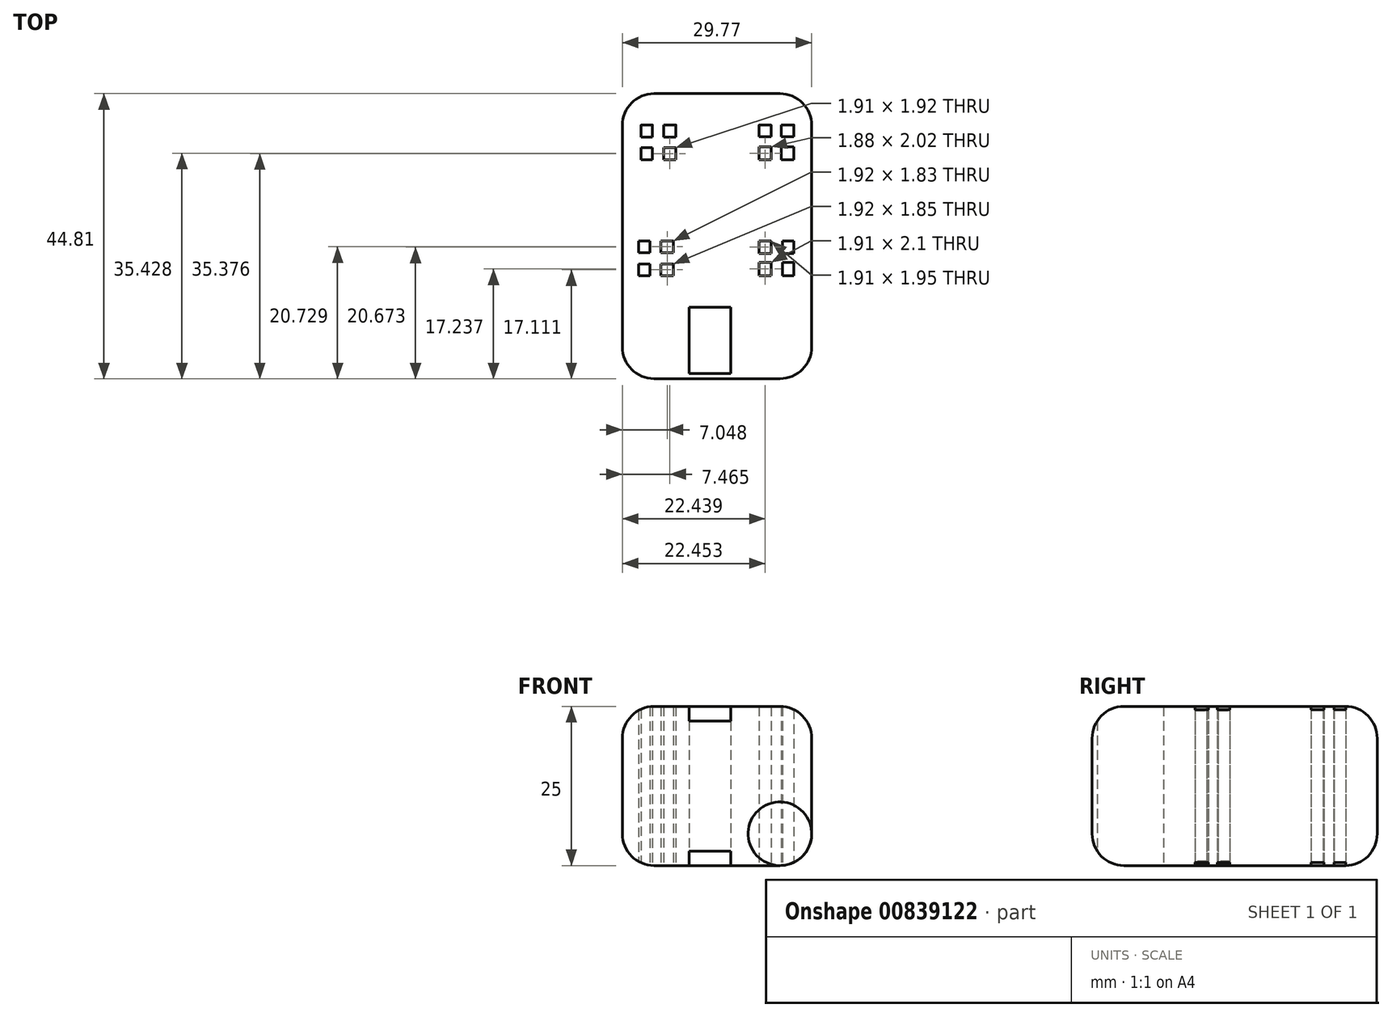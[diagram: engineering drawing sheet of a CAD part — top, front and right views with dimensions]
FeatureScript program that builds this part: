
annotation { "Feature Type Name" : "Feature", "Feature Type Description" : "" }
export const myFeature = defineFeature(function(context is Context, id is Id, definition is map)
    precondition{}
    {
        {
            var Q0;
            Q0=qCreatedBy(makeId("Top.planeOp"),FACE);
            var sketch = newSketch(context, id + "F0", { "sketchPlane" : qUnion([Q0])});
            skLineSegment(sketch, "E0", {"start": v(-55.24, 44.8) * mm, "end": v(-55.24, 0) * mm});
            skLineSegment(sketch, "E1", {"start": v(-55.24, 0) * mm, "end": v(-25.47, 0) * mm});
            skLineSegment(sketch, "E2", {"start": v(-25.47, 0) * mm, "end": v(-25.47, 44.2) * mm});
            skLineSegment(sketch, "E3", {"start": v(-55.24, 44.8) * mm, "end": v(-25.47, 44.8) * mm});
            skLineSegment(sketch, "E4", {"start": v(-25.47, 44.8) * mm, "end": v(-25.47, 44.2) * mm});
            skLineSegment(sketch, "E5.bottom", {"start": v(-44.76, 11.24) * mm, "end": v(-38.17, 11.24) * mm});
            skLineSegment(sketch, "E5.top", {"start": v(-44.76, 0) * mm, "end": v(-38.17, 0) * mm});
            skLineSegment(sketch, "E5.left", {"start": v(-44.76, 11.24) * mm, "end": v(-44.76, 0) * mm});
            skLineSegment(sketch, "E5.right", {"start": v(-38.17, 11.24) * mm, "end": v(-38.17, 0) * mm});
            skLineSegment(sketch, "E6.bottom", {"start": v(-52.28, 39.88) * mm, "end": v(-46.82, 39.88) * mm});
            skLineSegment(sketch, "E6.top", {"start": v(-52.28, 34.42) * mm, "end": v(-46.82, 34.42) * mm});
            skLineSegment(sketch, "E6.left", {"start": v(-52.28, 39.88) * mm, "end": v(-52.28, 34.42) * mm});
            skLineSegment(sketch, "E6.right", {"start": v(-46.82, 39.88) * mm, "end": v(-46.82, 34.42) * mm});
            skLineSegment(sketch, "E7.bottom", {"start": v(-28.28, 39.88) * mm, "end": v(-33.74, 39.88) * mm});
            skLineSegment(sketch, "E7.top", {"start": v(-28.28, 34.42) * mm, "end": v(-33.74, 34.42) * mm});
            skLineSegment(sketch, "E7.left", {"start": v(-28.28, 39.88) * mm, "end": v(-28.28, 34.42) * mm});
            skLineSegment(sketch, "E7.right", {"start": v(-33.74, 39.88) * mm, "end": v(-33.74, 34.42) * mm});
            skLineSegment(sketch, "E8.bottom", {"start": v(-52.7, 21.65) * mm, "end": v(-47.23, 21.65) * mm});
            skLineSegment(sketch, "E8.top", {"start": v(-52.7, 16.19) * mm, "end": v(-47.23, 16.19) * mm});
            skLineSegment(sketch, "E8.left", {"start": v(-52.7, 21.65) * mm, "end": v(-52.7, 16.19) * mm});
            skLineSegment(sketch, "E8.right", {"start": v(-47.23, 21.65) * mm, "end": v(-47.23, 16.19) * mm});
            skLineSegment(sketch, "E9.bottom", {"start": v(-28.28, 21.65) * mm, "end": v(-33.74, 21.65) * mm});
            skLineSegment(sketch, "E9.top", {"start": v(-28.28, 16.19) * mm, "end": v(-33.74, 16.19) * mm});
            skLineSegment(sketch, "E9.left", {"start": v(-28.28, 21.65) * mm, "end": v(-28.28, 16.19) * mm});
            skLineSegment(sketch, "E9.right", {"start": v(-33.74, 21.65) * mm, "end": v(-33.74, 16.19) * mm});
            skLineSegment(sketch, "E10.bottom", {"start": v(-49.55, 39.88) * mm, "end": v(-49.55, 39.88) * mm});
            skLineSegment(sketch, "E10.top", {"start": v(-49.55, 34.42) * mm, "end": v(-49.55, 34.42) * mm});
            skLineSegment(sketch, "E11.left", {"start": v(-52.28, 37.15) * mm, "end": v(-52.28, 37.15) * mm});
            skLineSegment(sketch, "E11.right", {"start": v(-46.82, 37.15) * mm, "end": v(-46.82, 37.15) * mm});
            skLineSegment(sketch, "E12", {"start": v(-50.88, 21.65) * mm, "end": v(-50.88, 16.19) * mm});
            skLineSegment(sketch, "E13", {"start": v(-50.88, 16.19) * mm, "end": v(-49.15, 16.19) * mm});
            skLineSegment(sketch, "E14", {"start": v(-49.15, 16.19) * mm, "end": v(-49.15, 21.65) * mm});
            skLineSegment(sketch, "E15", {"start": v(-50.5, 39.88) * mm, "end": v(-50.5, 34.42) * mm});
            skLineSegment(sketch, "E16", {"start": v(-50.5, 34.42) * mm, "end": v(-48.73, 34.42) * mm});
            skLineSegment(sketch, "E17", {"start": v(-48.73, 34.42) * mm, "end": v(-48.73, 39.88) * mm});
            skLineSegment(sketch, "E18", {"start": v(-31.86, 39.88) * mm, "end": v(-31.86, 34.42) * mm});
            skLineSegment(sketch, "E19", {"start": v(-31.86, 34.42) * mm, "end": v(-30.23, 34.42) * mm});
            skLineSegment(sketch, "E20", {"start": v(-30.23, 34.42) * mm, "end": v(-30.23, 39.88) * mm});
            skLineSegment(sketch, "E21", {"start": v(-31.83, 21.65) * mm, "end": v(-31.83, 16.19) * mm});
            skLineSegment(sketch, "E22", {"start": v(-31.83, 16.19) * mm, "end": v(-30.07, 16.19) * mm});
            skLineSegment(sketch, "E23", {"start": v(-30.07, 16.19) * mm, "end": v(-30.07, 21.65) * mm});
            skLineSegment(sketch, "E24", {"start": v(-52.28, 37.94) * mm, "end": v(-46.82, 37.94) * mm});
            skLineSegment(sketch, "E25", {"start": v(-46.82, 36.33) * mm, "end": v(-52.28, 36.33) * mm});
            skLineSegment(sketch, "E26", {"start": v(-33.74, 38) * mm, "end": v(-28.28, 38) * mm});
            skLineSegment(sketch, "E27", {"start": v(-28.28, 38) * mm, "end": v(-28.28, 36.44) * mm});
            skLineSegment(sketch, "E28", {"start": v(-28.28, 36.44) * mm, "end": v(-33.74, 36.44) * mm});
            skLineSegment(sketch, "E29", {"start": v(-33.74, 36.44) * mm, "end": v(-33.67, 36.53) * mm});
            skLineSegment(sketch, "E30", {"start": v(-33.74, 19.7) * mm, "end": v(-28.28, 19.7) * mm});
            skLineSegment(sketch, "E31", {"start": v(-28.28, 19.7) * mm, "end": v(-28.28, 18.29) * mm});
            skLineSegment(sketch, "E32", {"start": v(-28.28, 18.29) * mm, "end": v(-33.74, 18.29) * mm});
            skLineSegment(sketch, "E33", {"start": v(-52.7, 19.81) * mm, "end": v(-47.23, 19.81) * mm});
            skLineSegment(sketch, "E34", {"start": v(-52.7, 18.04) * mm, "end": v(-47.23, 18.04) * mm});
            skPoint(sketch, "E35.startSnap0", {"position": v(-40.36, 44.8) * mm});
            skLineSegment(sketch, "E36", {"start": v(-44.76, 0.8) * mm, "end": v(-38.17, 0.8) * mm});
            skSolve(sketch);
        }
        {
            var Q0;
            {var subQ47=sQuery(id+"F0.wireOp",EDGE,"E36");var subQ54=sQuery(id+"F0.wireOp",EDGE,"E0");Q0=qUnion([makeQuery(id+"F0.imprint","IMPRINT",FACE,{"disambiguationData":[TD([[makeQuery(id+"F0.imprint","IMPRINT",EDGE,{"derivedFrom":subQ47}),-1.0]])]}),makeQuery(id+"F0.imprint","IMPRINT",FACE,{"disambiguationData":[TD([[makeQuery(id+"F0.imprint","IMPRINT",EDGE,{"derivedFrom":subQ54}),1.0]])]})]);}
            var Q1;
            {var subQ0=sQuery(id+"F0.wireOp",EDGE,"E32");var subQ1=sQuery(id+"F0.wireOp",EDGE,"E21");var subQ2=makeQuery(id+"F0.imprint","INTERSECT",VERTEX,{"derivedFrom":[subQ1,subQ0]});Q1=makeQuery(id+"F0.imprint","IMPRINT",FACE,{"disambiguationData":[TD([[makeQuery(id+"F0.imprint","IMPRINT",EDGE,{"disambiguationData":[TD([[subQ2,1.0]])],"derivedFrom":subQ1}),1.0]])]});}
            var Q2;
            {var subQ0=sQuery(id+"F0.wireOp",EDGE,"E21");var subQ1=sQuery(id+"F0.wireOp",EDGE,"E9.top");var subQ2=makeQuery(id+"F0.imprint","INTERSECT",VERTEX,{"derivedFrom":[subQ1,subQ0]});Q2=makeQuery(id+"F0.imprint","IMPRINT",FACE,{"disambiguationData":[TD([[makeQuery(id+"F0.imprint","IMPRINT",EDGE,{"disambiguationData":[TD([[subQ2,1.0]])],"derivedFrom":subQ1}),-1.0]])]});}
            var Q3;
            {var subQ0=sQuery(id+"F0.wireOp",EDGE,"E32");var subQ1=sQuery(id+"F0.wireOp",EDGE,"E9.right");var subQ2=makeQuery(id+"F0.imprint","INTERSECT",VERTEX,{"derivedFrom":[subQ1,subQ0]});Q3=makeQuery(id+"F0.imprint","IMPRINT",FACE,{"disambiguationData":[TD([[makeQuery(id+"F0.imprint","IMPRINT",EDGE,{"disambiguationData":[TD([[subQ2,1.0]])],"derivedFrom":subQ1}),1.0]])]});}
            var Q4;
            {var subQ0=sQuery(id+"F0.wireOp",EDGE,"E21");var subQ1=sQuery(id+"F0.wireOp",EDGE,"E9.bottom");var subQ2=makeQuery(id+"F0.imprint","INTERSECT",VERTEX,{"derivedFrom":[subQ1,subQ0]});Q4=makeQuery(id+"F0.imprint","IMPRINT",FACE,{"disambiguationData":[TD([[makeQuery(id+"F0.imprint","IMPRINT",EDGE,{"disambiguationData":[TD([[subQ2,1.0]])],"derivedFrom":subQ1}),1.0]])]});}
            var Q5;
            {var subQ0=sQuery(id+"F0.wireOp",EDGE,"E32");var subQ1=sQuery(id+"F0.wireOp",EDGE,"E9.left");var subQ2=makeQuery(id+"F0.imprint","INTERSECT",VERTEX,{"derivedFrom":[subQ1,subQ0]});Q5=makeQuery(id+"F0.imprint","IMPRINT",FACE,{"disambiguationData":[TD([[makeQuery(id+"F0.imprint","IMPRINT",EDGE,{"disambiguationData":[TD([[subQ2,1.0]])],"derivedFrom":subQ1}),-1.0]])]});}
            var Q6;
            {var subQ0=sQuery(id+"F0.wireOp",EDGE,"E28");var subQ1=sQuery(id+"F0.wireOp",EDGE,"E18");var subQ2=makeQuery(id+"F0.imprint","INTERSECT",VERTEX,{"derivedFrom":[subQ1,subQ0]});Q6=makeQuery(id+"F0.imprint","IMPRINT",FACE,{"disambiguationData":[TD([[makeQuery(id+"F0.imprint","IMPRINT",EDGE,{"disambiguationData":[TD([[subQ2,1.0]])],"derivedFrom":subQ1}),1.0]])]});}
            var Q7;
            {var subQ0=sQuery(id+"F0.wireOp",EDGE,"E18");var subQ1=sQuery(id+"F0.wireOp",EDGE,"E7.bottom");var subQ2=makeQuery(id+"F0.imprint","INTERSECT",VERTEX,{"derivedFrom":[subQ1,subQ0]});Q7=makeQuery(id+"F0.imprint","IMPRINT",FACE,{"disambiguationData":[TD([[makeQuery(id+"F0.imprint","IMPRINT",EDGE,{"disambiguationData":[TD([[subQ2,1.0]])],"derivedFrom":subQ1}),1.0]])]});}
            var Q8;
            {var subQ0=sQuery(id+"F0.wireOp",EDGE,"E28");var subQ1=sQuery(id+"F0.wireOp",EDGE,"E7.left");var subQ2=makeQuery(id+"F0.imprint","INTERSECT",VERTEX,{"derivedFrom":[subQ1,subQ0]});Q8=makeQuery(id+"F0.imprint","IMPRINT",FACE,{"disambiguationData":[TD([[makeQuery(id+"F0.imprint","IMPRINT",EDGE,{"disambiguationData":[TD([[subQ2,1.0]])],"derivedFrom":subQ1}),-1.0]])]});}
            var Q9;
            {var subQ0=sQuery(id+"F0.wireOp",EDGE,"E18");var subQ1=sQuery(id+"F0.wireOp",EDGE,"E7.top");var subQ2=makeQuery(id+"F0.imprint","INTERSECT",VERTEX,{"derivedFrom":[subQ1,subQ0]});Q9=makeQuery(id+"F0.imprint","IMPRINT",FACE,{"disambiguationData":[TD([[makeQuery(id+"F0.imprint","IMPRINT",EDGE,{"disambiguationData":[TD([[subQ2,1.0]])],"derivedFrom":subQ1}),-1.0]])]});}
            var Q10;
            {var subQ0=sQuery(id+"F0.wireOp",EDGE,"E28");var subQ1=sQuery(id+"F0.wireOp",EDGE,"E7.right");var subQ2=makeQuery(id+"F0.imprint","INTERSECT",VERTEX,{"derivedFrom":[subQ1,subQ0]});Q10=makeQuery(id+"F0.imprint","IMPRINT",FACE,{"disambiguationData":[TD([[makeQuery(id+"F0.imprint","IMPRINT",EDGE,{"disambiguationData":[TD([[subQ2,1.0]])],"derivedFrom":subQ1}),1.0]])]});}
            var Q11;
            {var subQ0=sQuery(id+"F0.wireOp",EDGE,"E25");var subQ1=sQuery(id+"F0.wireOp",EDGE,"E6.left");var subQ2=makeQuery(id+"F0.imprint","INTERSECT",VERTEX,{"derivedFrom":[subQ1,subQ0]});Q11=makeQuery(id+"F0.imprint","IMPRINT",FACE,{"disambiguationData":[TD([[makeQuery(id+"F0.imprint","IMPRINT",EDGE,{"disambiguationData":[TD([[subQ2,1.0]])],"derivedFrom":subQ1}),1.0]])]});}
            var Q12;
            {var subQ0=sQuery(id+"F0.wireOp",EDGE,"E25");var subQ1=sQuery(id+"F0.wireOp",EDGE,"E15");var subQ2=makeQuery(id+"F0.imprint","INTERSECT",VERTEX,{"derivedFrom":[subQ1,subQ0]});Q12=makeQuery(id+"F0.imprint","IMPRINT",FACE,{"disambiguationData":[TD([[makeQuery(id+"F0.imprint","IMPRINT",EDGE,{"disambiguationData":[TD([[subQ2,1.0]])],"derivedFrom":subQ1}),1.0]])]});}
            var Q13;
            {var subQ0=sQuery(id+"F0.wireOp",EDGE,"E17");var subQ1=sQuery(id+"F0.wireOp",EDGE,"E6.bottom");var subQ2=makeQuery(id+"F0.imprint","INTERSECT",VERTEX,{"derivedFrom":[subQ1,subQ0]});Q13=makeQuery(id+"F0.imprint","IMPRINT",FACE,{"disambiguationData":[TD([[makeQuery(id+"F0.imprint","IMPRINT",EDGE,{"disambiguationData":[TD([[subQ2,1.0]])],"derivedFrom":subQ1}),-1.0]])]});}
            var Q14;
            {var subQ0=sQuery(id+"F0.wireOp",EDGE,"E17");var subQ1=sQuery(id+"F0.wireOp",EDGE,"E6.top");var subQ2=makeQuery(id+"F0.imprint","INTERSECT",VERTEX,{"derivedFrom":[subQ1,subQ0]});Q14=makeQuery(id+"F0.imprint","IMPRINT",FACE,{"disambiguationData":[TD([[makeQuery(id+"F0.imprint","IMPRINT",EDGE,{"disambiguationData":[TD([[subQ2,1.0]])],"derivedFrom":subQ1}),1.0]])]});}
            var Q15;
            {var subQ0=sQuery(id+"F0.wireOp",EDGE,"E25");var subQ1=sQuery(id+"F0.wireOp",EDGE,"E6.right");var subQ2=makeQuery(id+"F0.imprint","INTERSECT",VERTEX,{"derivedFrom":[subQ1,subQ0]});Q15=makeQuery(id+"F0.imprint","IMPRINT",FACE,{"disambiguationData":[TD([[makeQuery(id+"F0.imprint","IMPRINT",EDGE,{"disambiguationData":[TD([[subQ2,1.0]])],"derivedFrom":subQ1}),-1.0]])]});}
            var Q16;
            {var subQ0=sQuery(id+"F0.wireOp",EDGE,"E14");var subQ1=sQuery(id+"F0.wireOp",EDGE,"E8.top");var subQ2=makeQuery(id+"F0.imprint","INTERSECT",VERTEX,{"derivedFrom":[subQ1,subQ0]});Q16=makeQuery(id+"F0.imprint","IMPRINT",FACE,{"disambiguationData":[TD([[makeQuery(id+"F0.imprint","IMPRINT",EDGE,{"disambiguationData":[TD([[subQ2,1.0]])],"derivedFrom":subQ1}),1.0]])]});}
            var Q17;
            {var subQ0=sQuery(id+"F0.wireOp",EDGE,"E34");var subQ1=sQuery(id+"F0.wireOp",EDGE,"E12");var subQ2=makeQuery(id+"F0.imprint","INTERSECT",VERTEX,{"derivedFrom":[subQ1,subQ0]});Q17=makeQuery(id+"F0.imprint","IMPRINT",FACE,{"disambiguationData":[TD([[makeQuery(id+"F0.imprint","IMPRINT",EDGE,{"disambiguationData":[TD([[subQ2,1.0]])],"derivedFrom":subQ1}),1.0]])]});}
            var Q18;
            {var subQ0=sQuery(id+"F0.wireOp",EDGE,"E14");var subQ1=sQuery(id+"F0.wireOp",EDGE,"E8.bottom");var subQ2=makeQuery(id+"F0.imprint","INTERSECT",VERTEX,{"derivedFrom":[subQ1,subQ0]});Q18=makeQuery(id+"F0.imprint","IMPRINT",FACE,{"disambiguationData":[TD([[makeQuery(id+"F0.imprint","IMPRINT",EDGE,{"disambiguationData":[TD([[subQ2,1.0]])],"derivedFrom":subQ1}),-1.0]])]});}
            var Q19;
            {var subQ0=sQuery(id+"F0.wireOp",EDGE,"E34");var subQ1=sQuery(id+"F0.wireOp",EDGE,"E8.left");var subQ2=makeQuery(id+"F0.imprint","INTERSECT",VERTEX,{"derivedFrom":[subQ1,subQ0]});Q19=makeQuery(id+"F0.imprint","IMPRINT",FACE,{"disambiguationData":[TD([[makeQuery(id+"F0.imprint","IMPRINT",EDGE,{"disambiguationData":[TD([[subQ2,1.0]])],"derivedFrom":subQ1}),1.0]])]});}
            var Q20;
            {var subQ0=sQuery(id+"F0.wireOp",EDGE,"E34");var subQ1=sQuery(id+"F0.wireOp",EDGE,"E8.right");var subQ2=makeQuery(id+"F0.imprint","INTERSECT",VERTEX,{"derivedFrom":[subQ1,subQ0]});Q20=makeQuery(id+"F0.imprint","IMPRINT",FACE,{"disambiguationData":[TD([[makeQuery(id+"F0.imprint","IMPRINT",EDGE,{"disambiguationData":[TD([[subQ2,1.0]])],"derivedFrom":subQ1}),-1.0]])]});}
            extrude(context, id + "F1", {"entities" : qUnion([Q0, Q1, Q2, Q3, Q4, Q5, Q6, Q7, Q8, Q9, Q10, Q11, Q12, Q13, Q14, Q15, Q16, Q17, Q18, Q19, Q20]), "depth" : 25 * mm, "offsetDistance" : 25 * mm});
        }
        {
            var Q0;
            Q0=makeQuery(id+"F1.opExtrude","CAP_EDGE",EDGE,{"disambiguationData":[OSD([sQuery(id+"F0.wireOp",EDGE,"E2"),sQuery(id+"F0.wireOp",EDGE,"E4")])],"isStart":true});
            var Q1;
            Q1=makeQuery(id+"F1.opExtrude","SWEPT_EDGE",EDGE,{"disambiguationData":[OSD([sQuery(id+"F0.wireOp",EDGE,"E3"),sQuery(id+"F0.wireOp",EDGE,"E4")])]});
            var Q2;
            Q2=makeQuery(id+"F1.opExtrude","CAP_EDGE",EDGE,{"disambiguationData":[OSD([sQuery(id+"F0.wireOp",EDGE,"E2"),sQuery(id+"F0.wireOp",EDGE,"E4")])],"isStart":false});
            var Q3;
            Q3=makeQuery(id+"F1.opExtrude","CAP_EDGE",EDGE,{"disambiguationData":[OSD([sQuery(id+"F0.wireOp",EDGE,"E3")])],"isStart":true});
            var Q4;
            Q4=makeQuery(id+"F1.opExtrude","CAP_EDGE",EDGE,{"disambiguationData":[OSD([sQuery(id+"F0.wireOp",EDGE,"E0")])],"isStart":true});
            var Q5;
            Q5=makeQuery(id+"F1.opExtrude","CAP_EDGE",EDGE,{"disambiguationData":[OSD([sQuery(id+"F0.wireOp",EDGE,"E0")])],"isStart":false});
            var Q6;
            Q6=makeQuery(id+"F1.opExtrude","CAP_EDGE",EDGE,{"disambiguationData":[OSD([sQuery(id+"F0.wireOp",EDGE,"E3")])],"isStart":false});
            var Q7;
            Q7=makeQuery(id+"F1.opExtrude","SWEPT_EDGE",EDGE,{"disambiguationData":[OSD([sQuery(id+"F0.wireOp",EDGE,"E0"),sQuery(id+"F0.wireOp",EDGE,"E3")])]});
            var Q8;
            Q8=makeQuery(id+"F1.opExtrude","SWEPT_EDGE",EDGE,{"disambiguationData":[OSD([sQuery(id+"F0.wireOp",EDGE,"E0"),sQuery(id+"F0.wireOp",EDGE,"E1")])]});
            var Q9;
            Q9=makeQuery(id+"F1.opExtrude","CAP_EDGE",EDGE,{"disambiguationData":[OSD([sQuery(id+"F0.wireOp",EDGE,"E1")])],"isStart":false});
            var Q10;
            Q10=makeQuery(id+"F1.opExtrude","SWEPT_EDGE",EDGE,{"disambiguationData":[OSD([sQuery(id+"F0.wireOp",EDGE,"E1"),sQuery(id+"F0.wireOp",EDGE,"E2")])]});
            var Q11;
            Q11=makeQuery(id+"F1.opExtrude","CAP_EDGE",EDGE,{"disambiguationData":[OSD([sQuery(id+"F0.wireOp",EDGE,"E1")])],"isStart":true});
            fillet(context, id + "F2", {"entities" : qUnion([Q0, Q1, Q2, Q3, Q4, Q5, Q6, Q7, Q8, Q9, Q10, Q11]), "radius" : 5 * mm, "tangentPropagation" : true, "allowEdgeOverflow" : false});
        }
    });
